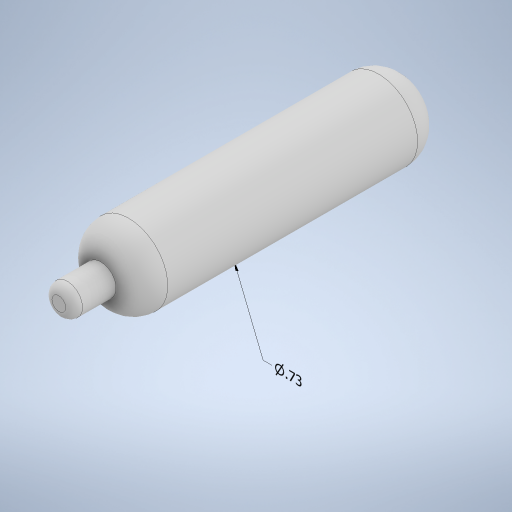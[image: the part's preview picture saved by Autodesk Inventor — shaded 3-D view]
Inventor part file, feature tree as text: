
AUTODESK INVENTOR PART (.ipt)
format: ipt  version: 2023 (Build 270158000, 158)  size: 258,560 bytes
history: native  units: in
note: dims shown in document units (in); Inventor stores cm internally (conversion verified against a paired STEP export)
features: fillet x3, other x2, extrude x2, sketch x2
ambient origin geometry x8: Origin, YZ Plane, XZ Plane, XY Plane, X Axis, Y Axis, Z Axis, Center Point
bodies: Solid1 (feature_tree)
feature tree (9):
  other  "Annotations"
  extrude  "Extrusion1"  Depth=2.874in TaperAngle=0.0deg
  extrude  "Extrusion2"  Depth=0.3937in TaperAngle=0.0deg
  fillet  "Fillet1"  Radius=0.2662in
  fillet  "Fillet2"  Radius=0.0787in
  fillet  "Fillet3"  Radius=0.2662in
  sketch  "Sketch1"  dims[d0=0.7323in d1=2.874in d2=0.0in]
  sketch  "Sketch2"  dims[d3=0.2874in d4=0.3937in d5=0.0in d6=0.2662in d7=0.0787in d8=0.2662in d10=0.2508in d11=0.1193in d12=0.7323in d9=2.0175in d13=0.0in d14=0.0in d15=0.0in d16=0.0in]
  other  "Diameter Dimension 1"
